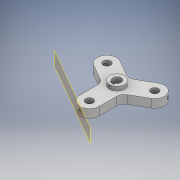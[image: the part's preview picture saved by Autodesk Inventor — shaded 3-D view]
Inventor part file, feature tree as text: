
AUTODESK INVENTOR PART (.ipt)
format: ipt  version: 2019 (Build 230136000, 136)  size: 215,552 bytes
history: native  units: mm
features: plane x6, sketch x6, other x4, extrude x4, hole x2, projected_geometry x2, pattern_circular x1
ambient origin geometry x8: Origin, YZ Plane, XZ Plane, XY Plane, X Axis, Y Axis, Z Axis, Center Point
bodies: Body1 (feature_tree)
feature tree (25):
  other  "實體1"
  extrude  "擠出1"  Depth=33.0mm
  plane  "工作平面1"
  plane  "工作平面2"
  plane  "工作平面3"
  hole  "孔1"  [1 undecoded]
  extrude  "擠出2"  Depth=33.0mm
  extrude  "擠出3"  Depth=9.0mm
  plane  "工作平面4"
  hole  "孔2"  [1 undecoded]
  plane  "工作平面5"
  plane  "工作平面6"
  extrude  "擠出4"  Depth=7.0mm
  pattern_circular  "環形陣列2"  [2 undecoded]
  other  "螺紋1"
  other  "螺紋2"
  other  "螺紋3"
  sketch  "草圖1"
  sketch  "草圖2"
  sketch  "草圖3"
  sketch  "草圖4"
  projected_geometry  "投影迴路1"
  sketch  "草圖5"
  sketch  "草圖6"
  projected_geometry  "投影迴路2"
note: 4 required parameter values undecoded (feature->parameter linkage not recoverable at this tier; creation-order binding heuristic only, values carry confidence <= 0.55)
